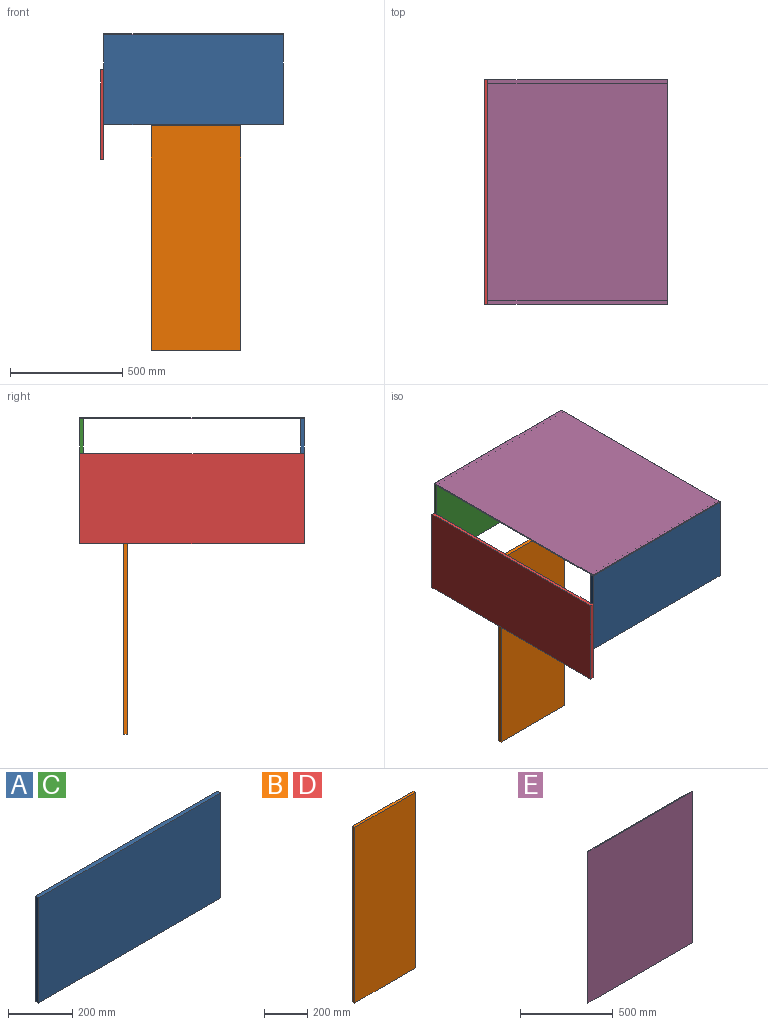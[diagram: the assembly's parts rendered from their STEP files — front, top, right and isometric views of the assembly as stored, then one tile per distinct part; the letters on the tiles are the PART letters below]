
ASSEMBLY  parts=5 mates=9
PART A: 6 faces, bbox 800x15x400 mm
  f0: plane 400x15mm, normal (-1,0,0), area 6000mm2, adj f1,f3,f4,f5
  f1: plane 800x15mm, normal (0,0,-1), area 12000mm2, adj f0,f2,f4,f5
  f2: plane 400x15mm, normal (1,0,0), area 6000mm2, adj f1,f3,f4,f5
  f3: plane 800x15mm, normal (0,0,1), area 12000mm2, adj f0,f2,f4,f5
  f4: plane 800x400mm, normal (0,-1,0), area 320000mm2, adj f0,f1,f2,f3
  f5: plane 800x400mm, normal (0,1,0), area 320000mm2, adj f0,f1,f2,f3
PART B: 6 faces, bbox 400x15x1000 mm
  f0: plane 1000x15mm, normal (-1,0,0), area 15000mm2, adj f1,f3,f4,f5
  f1: plane 400x15mm, normal (0,0,-1), area 6000mm2, adj f0,f2,f4,f5
  f2: plane 1000x15mm, normal (1,0,0), area 15000mm2, adj f1,f3,f4,f5
  f3: plane 400x15mm, normal (0,0,1), area 6000mm2, adj f0,f2,f4,f5
  f4: plane 1000x400mm, normal (0,-1,0), area 400000mm2, adj f0,f1,f2,f3
  f5: plane 1000x400mm, normal (0,1,0), area 400000mm2, adj f0,f1,f2,f3
PART C: same geometry as A
PART D: same geometry as B
PART E: 6 faces, bbox 800x5x1000 mm
  f0: plane 1000x5mm, normal (-1,0,0), area 5000mm2, adj f1,f3,f4,f5
  f1: plane 800x5mm, normal (0,0,-1), area 4000mm2, adj f0,f2,f4,f5
  f2: plane 1000x5mm, normal (1,0,0), area 5000mm2, adj f1,f3,f4,f5
  f3: plane 800x5mm, normal (0,0,1), area 4000mm2, adj f0,f2,f4,f5
  f4: plane 1000x800mm, normal (0,-1,0), area 800000mm2, adj f0,f1,f2,f3
  f5: plane 1000x800mm, normal (0,1,0), area 800000mm2, adj f0,f1,f2,f3
PLACE A t=(-875.61,-385.49,-112.71)mm
PLACE B t=(-665.73,403.53,-1119)mm
PLACE C t=(-875.61,599.51,-112.71)mm
PLACE D rot(axis=(0.58,-0.58,0.58),120deg) t=(-890.61,599.51,-269.23)mm
PLACE E rot(axis=(1,0,0),90deg) t=(-875.61,599.51,292.29)mm
MATE planar E.f4 <-> A.f3  axis (0,0,-1) through (-875.61,-400.49,287.29)mm
MATE planar A.f4 <-> E.f3  axis (0,-1,0) through (-475.61,-400.49,87.29)mm
MATE planar D.f3 <-> A.f4  axis (0,-1,0) through (-883.11,-400.49,-69.23)mm
MATE planar C.f3 <-> E.f4  axis (0,0,1) through (-475.61,592.01,287.29)mm
MATE planar D.f4 <-> A.f0  axis (1,0,0) through (-875.61,99.51,-69.23)mm
MATE planar E.f1 <-> C.f5  axis (0,1,0) through (-475.61,599.51,289.79)mm
MATE planar E.f0 <-> C.f0  axis (-1,0,0) through (-875.61,99.51,289.79)mm
MATE planar C.f4 <-> E.f1  axis (0,-1,0) through (-475.61,584.51,87.29)mm
MATE planar E.f0 <-> A.f0  axis (-1,0,0) through (-875.61,99.51,289.79)mm
